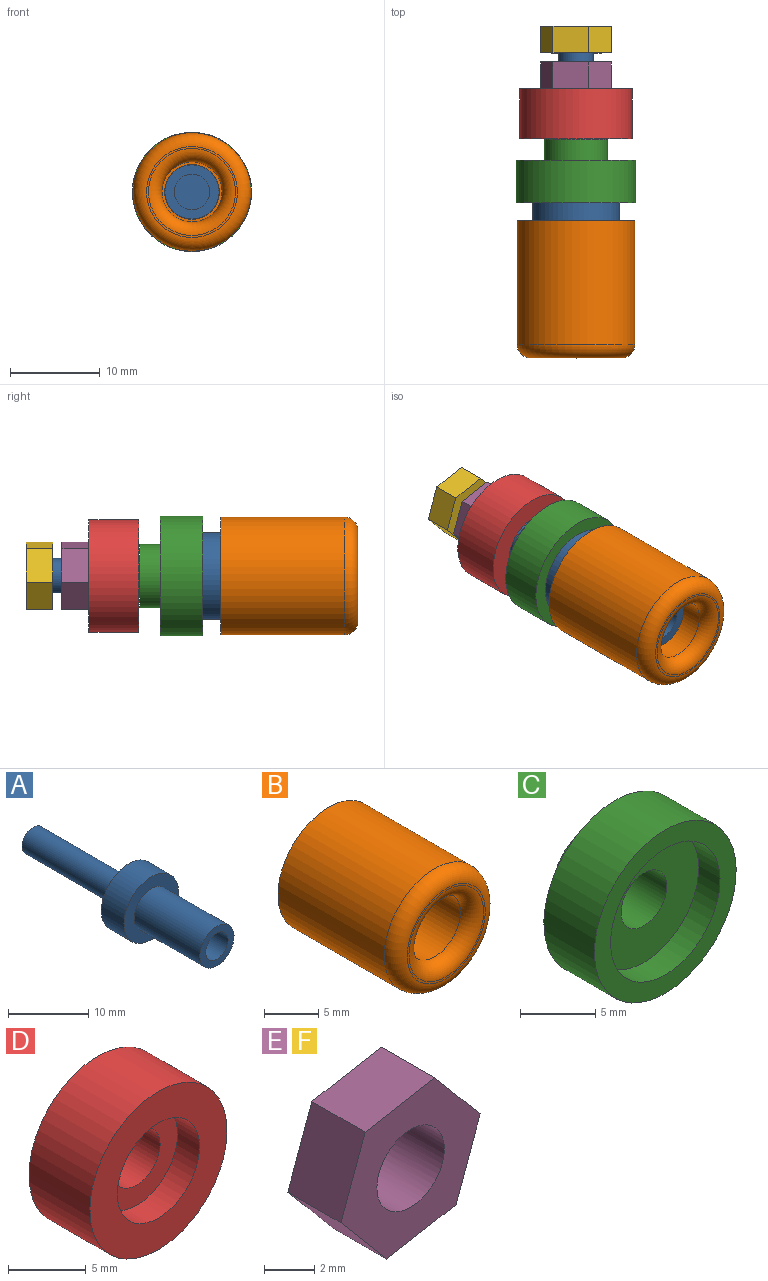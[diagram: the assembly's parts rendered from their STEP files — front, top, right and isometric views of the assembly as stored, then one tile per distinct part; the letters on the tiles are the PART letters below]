
ASSEMBLY  parts=6 mates=5
PART A: 9 faces, bbox 9.7x32.5x9.7 mm
  f0: cylinder r=4.83mm len=9.65mm, axis (0,1,0), area 121.3mm2, adj f1,f2
  f1: plane 9.65x9.65mm, normal (0,-1,0), area 44.5mm2, adj f0,f5
  f2: plane 9.65x9.65mm, normal (0,1,0), area 61.2mm2, adj f0,f3
  f3: cylinder r=1.95mm len=16.9mm, axis (0,-1,0), area 207.1mm2, adj f2,f4
  f4: plane 3.9x3.9mm, normal (0,1,0), area 11.9mm2, adj f3
  f5: cylinder r=3.02mm len=11.6mm, axis (0,1,0), area 220.1mm2, adj f1,f6
  f6: plane 6.04x6.04mm, normal (0,-1,0), area 16.4mm2, adj f5,f7
  f7: cylinder r=1.98mm len=13.4mm, axis (0,-1,0), area 166.3mm2, adj f6,f8
  f8: plane 3.95x3.95mm, normal (0,-1,0), area 12.3mm2, adj f7
PART B: 8 faces, bbox 14.2x15.3x14.2 mm
  f0: cylinder r=3.05mm len=6.1mm, axis (0,1,0), area 103.5mm2, adj f3,f4
  f1: cylinder r=6.56mm len=13.8mm, axis (0,1,0), area 569.2mm2, adj f3,f7
  f2: plane 10.13x10.13mm, normal (0,-1,0), area 6.7mm2, adj f6,f7
  f3: plane 13.13x13.13mm, normal (0,1,0), area 106.2mm2, adj f0,f1
  f4: plane 6.7x6.7mm, normal (0,-1,0), area 6mm2, adj f0,f5
  f5: cylinder r=3.35mm len=8.4mm, axis (0,-1,0), area 176.8mm2, adj f4,f6
  f6: torus R=4.85mm, axis (0,-1,0), area 57.7mm2, adj f2,f5
  f7: torus R=5.07mm, axis (0,-1,0), area 89.1mm2, adj f1,f2
PART C: 8 faces, bbox 13.3x7.1x13.3 mm
  f0: cylinder r=2.15mm len=5.05mm, axis (0,1,0), area 68.2mm2, adj f5,f7
  f1: cylinder r=6.65mm len=13.3mm, axis (0,1,0), area 198.5mm2, adj f2,f3
  f2: plane 13.3x13.3mm, normal (0,-1,0), area 56mm2, adj f1,f6
  f3: plane 13.3x13.3mm, normal (0,1,0), area 99.9mm2, adj f1,f4
  f4: cylinder r=3.52mm len=7.05mm, axis (0,-1,0), area 50.9mm2, adj f3,f5
  f5: plane 7.05x7.05mm, normal (0,1,0), area 24.5mm2, adj f0,f4
  f6: cylinder r=5.14mm len=10.28mm, axis (0,-1,0), area 64.6mm2, adj f2,f7
  f7: plane 10.28x10.28mm, normal (0,-1,0), area 68.4mm2, adj f0,f6
PART D: 6 faces, bbox 12.5x5.6x12.5 mm
  f0: cylinder r=2.15mm len=4.3mm, axis (0,1,0), area 48mm2, adj f2,f5
  f1: cylinder r=6.25mm len=12.5mm, axis (0,-1,0), area 217.9mm2, adj f2,f3
  f2: plane 12.5x12.5mm, normal (0,1,0), area 108.2mm2, adj f0,f1
  f3: plane 12.5x12.5mm, normal (0,-1,0), area 78.6mm2, adj f1,f4
  f4: cylinder r=3.75mm len=7.5mm, axis (0,-1,0), area 47.1mm2, adj f3,f5
  f5: plane 7.5x7.5mm, normal (0,-1,0), area 29.6mm2, adj f0,f4
PART E: 9 faces, bbox 7.8x3x7.5 mm
  f0: plane 3.75x3mm, normal (-0.94,0,0.34), area 12mm2, adj f1,f5,f6,f7
  f1: plane 3.05x3mm, normal (-0.77,0,-0.64), area 12mm2, adj f0,f2,f6,f7
  f2: plane 3.92x3mm, normal (0.17,0,-0.98), area 12mm2, adj f1,f3,f6,f7
  f3: plane 3.75x3mm, normal (0.94,0,-0.34), area 12mm2, adj f2,f4,f6,f7
  f4: plane 3.05x3mm, normal (0.77,0,0.64), area 12mm2, adj f3,f5,f6,f7
  f5: plane 3.92x3mm, normal (-0.17,0,0.98), area 12mm2, adj f0,f4,f6,f7
  f6: plane 7.84x7.49mm, normal (0,1,0), area 29.9mm2, adj f0,f1,f2,f3,f4,f5,f8
  f7: plane 7.84x7.49mm, normal (0,-1,0), area 29.9mm2, adj f0,f1,f2,f3,f4,f5,f8
  f8: cylinder r=1.9mm len=3.8mm, axis (0,1,0), area 35.8mm2, adj f6,f7
PART F: same geometry as E
PLACE A t=(-7.45,26.4,-8.02)mm
PLACE B t=(-7.45,47.4,-8.02)mm
PLACE C t=(-7.45,4.15,-8.02)mm
PLACE D t=(-7.45,-3.15,-8.02)mm
PLACE E t=(-7.45,-22.6,-8.02)mm
PLACE F t=(-7.45,-18.6,-8.02)mm
MATE fastened F.f8 <-> E.f8  axis (0,-1,0) through (-7.45,16.1,-8.02)mm
MATE fastened C.f1 <-> D.f4  axis (0,1,0) through (-7.45,4.15,-8.02)mm
MATE fastened B.f1 <-> A.f0  axis (0,1,0) through (-7.45,-2.6,-8.02)mm
MATE fastened E.f8 <-> D.f0  axis (0,-1,0) through (-7.45,12.1,-8.02)mm
MATE fastened A.f3 <-> C.f0  axis (0,1,0) through (-7.45,1.4,-8.02)mm
